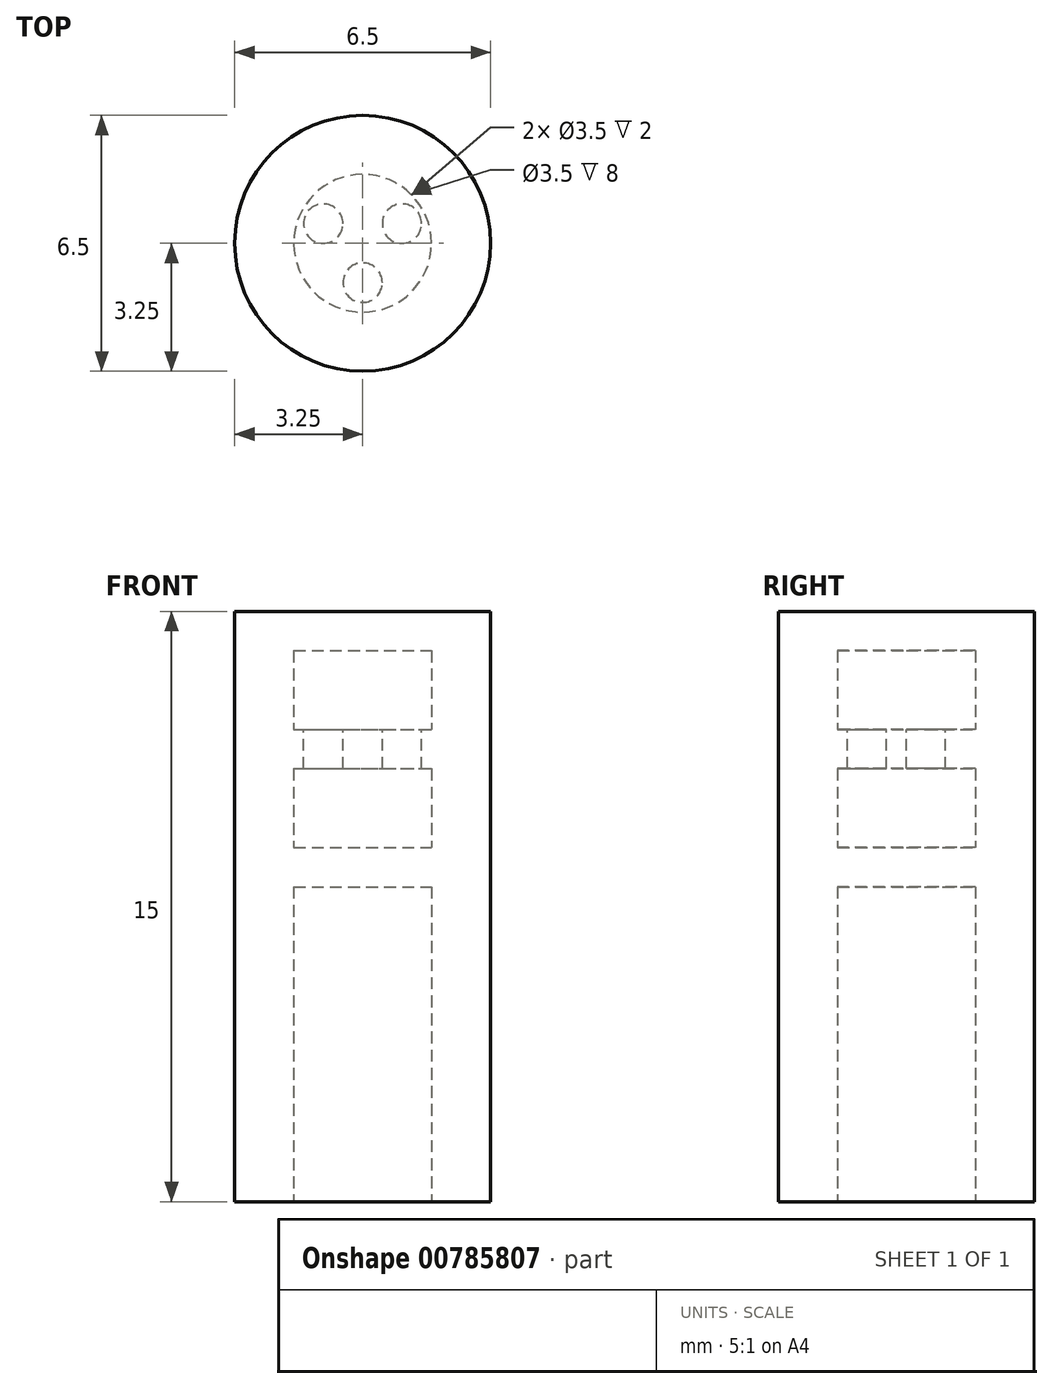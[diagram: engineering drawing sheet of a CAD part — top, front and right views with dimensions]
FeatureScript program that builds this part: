
annotation { "Feature Type Name" : "Feature", "Feature Type Description" : "" }
export const myFeature = defineFeature(function(context is Context, id is Id, definition is map)
    precondition{}
    {
        {
            var Q0;
            Q0=qCreatedBy(makeId("Top.planeOp"),FACE);
            var sketch = newSketch(context, id + "F0", { "sketchPlane" : qUnion([Q0])});
            skCircle(sketch, "E0", {"center": v(0, 0) * mm, "radius": 3.25 * mm});
            skSolve(sketch);
        }
        {
            var Q0;
            Q0 = qSketchRegion(id + "F0", true);
            extrude(context, id + "F1", {"entities" : qUnion([Q0]), "depth" : 15 * mm, "offsetDistance" : 25 * mm});
        }
        {
            var Q0;
            Q0=makeQuery(id+"F1.opExtrude","CAP_FACE",FACE,{"disambiguationData":[OSD([sQuery(id+"F0.wireOp",EDGE,"E0")])],"isStart":true});
            var sketch = newSketch(context, id + "F2", { "sketchPlane" : qUnion([Q0])});
            skCircle(sketch, "E1", {"center": v(0, 0) * mm, "radius": 1.75 * mm});
            skSolve(sketch);
        }
        {
            var Q0;
            Q0 = qSketchRegion(id + "F2", true);
            extrude(context, id + "F3", {"entities" : qUnion([Q0]), "operationType" : NewBodyOperationType.REMOVE, "oppositeDirection" : true, "depth" : 8 * mm, "offsetDistance" : 25 * mm});
        }
        {
            var Q0;
            Q0=makeQuery(id+"F3.boolean.opBoolean","COPY",FACE,{"derivedFrom":makeQuery(id+"F3.opExtrude","CAP_FACE",FACE,{"disambiguationData":[OSD([sQuery(id+"F2.wireOp",EDGE,"E1")])],"isStart":false})});
            cPlane(context, id + "F4", {"entities" : qUnion([Q0]), "cplaneType" : CPlaneType.OFFSET, "offset" : 1 * mm, "oppositeDirection" : true, "width" : 150 * mm, "height" : 150 * mm});
        }
        {
            var Q0;
            Q0=qCreatedBy(id+"F4.planeOp",FACE);
            var sketch = newSketch(context, id + "F5", { "sketchPlane" : qUnion([Q0])});
            skCircle(sketch, "E2.0", {"center": v(0, 0) * mm, "radius": 1.75 * mm});
            skSolve(sketch);
        }
        {
            var Q0;
            Q0 = qSketchRegion(id + "F5", true);
            extrude(context, id + "F6", {"entities" : qUnion([Q0]), "operationType" : NewBodyOperationType.REMOVE, "oppositeDirection" : true, "depth" : 2 * mm, "offsetDistance" : 25 * mm});
        }
        {
            var Q0;
            Q0=makeQuery(id+"F6.boolean.opBoolean","COPY",FACE,{"derivedFrom":makeQuery(id+"F6.opExtrude","CAP_FACE",FACE,{"disambiguationData":[OSD([sQuery(id+"F5.wireOp",EDGE,"E2.0")])],"isStart":false})});
            cPlane(context, id + "F7", {"entities" : qUnion([Q0]), "cplaneType" : CPlaneType.OFFSET, "offset" : 1 * mm, "oppositeDirection" : true, "width" : 150 * mm, "height" : 150 * mm});
        }
        {
            var Q0;
            Q0=qCreatedBy(id+"F7.planeOp",FACE);
            var sketch = newSketch(context, id + "F8", { "sketchPlane" : qUnion([Q0])});
            skCircle(sketch, "E3.0", {"center": v(0, 0) * mm, "radius": 1.75 * mm});
            skSolve(sketch);
        }
        {
            var Q0;
            Q0 = qSketchRegion(id + "F8", true);
            extrude(context, id + "F9", {"entities" : qUnion([Q0]), "operationType" : NewBodyOperationType.REMOVE, "oppositeDirection" : true, "depth" : 2 * mm, "offsetDistance" : 25 * mm});
        }
        {
            var Q0;
            Q0=qCreatedBy(id+"F7.planeOp",FACE);
            var sketch = newSketch(context, id + "F10", { "sketchPlane" : qUnion([Q0])});
            skCircle(sketch, "E4", {"center": v(-1, -0.5) * mm, "radius": 0.5 * mm});
            skCircle(sketch, "E5", {"center": v(1, -0.5) * mm, "radius": 0.5 * mm});
            skCircle(sketch, "E6", {"center": v(0, 1) * mm, "radius": 0.5 * mm});
            skSolve(sketch);
        }
        {
            var Q0;
            Q0 = qSketchRegion(id + "F10", true);
            extrude(context, id + "F11", {"entities" : qUnion([Q0]), "operationType" : NewBodyOperationType.REMOVE, "depth" : 1 * mm, "offsetDistance" : 25 * mm});
        }
    });
